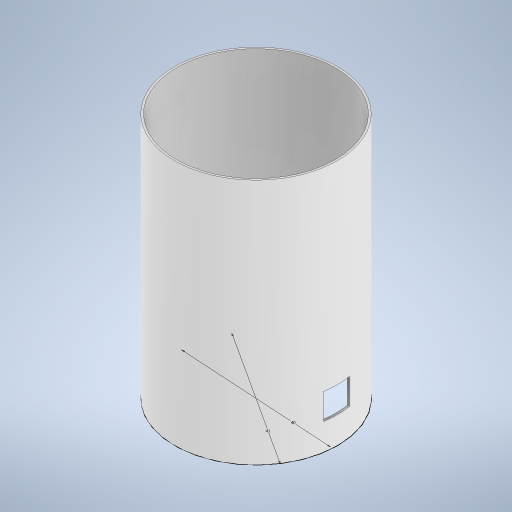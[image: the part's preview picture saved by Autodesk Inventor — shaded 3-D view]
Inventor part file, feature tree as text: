
AUTODESK INVENTOR PART (.ipt)
format: ipt  version: 2024 (Build 280153000, 153)  size: 240,640 bytes
history: native  units: in
note: dims shown in document units (in); Inventor stores cm internally (conversion verified against a paired STEP export)
features: sketch x2, extrude x1
ambient origin geometry x8: Origin, YZ Plane, XZ Plane, XY Plane, X Axis, Y Axis, Z Axis, Center Point
bodies: Solid2 (feature_tree), Solid1 (feature_tree)
feature tree (3):
  sketch  "Sketch1"  dims[d0=1.5748in d1=1.6142in]
  extrude  "Extrusion1"  Depth=1.6142in
  sketch  "Sketch2"  dims[d2=1.5748in d3=1.6142in d4=1.6535in d5=0.0in]
